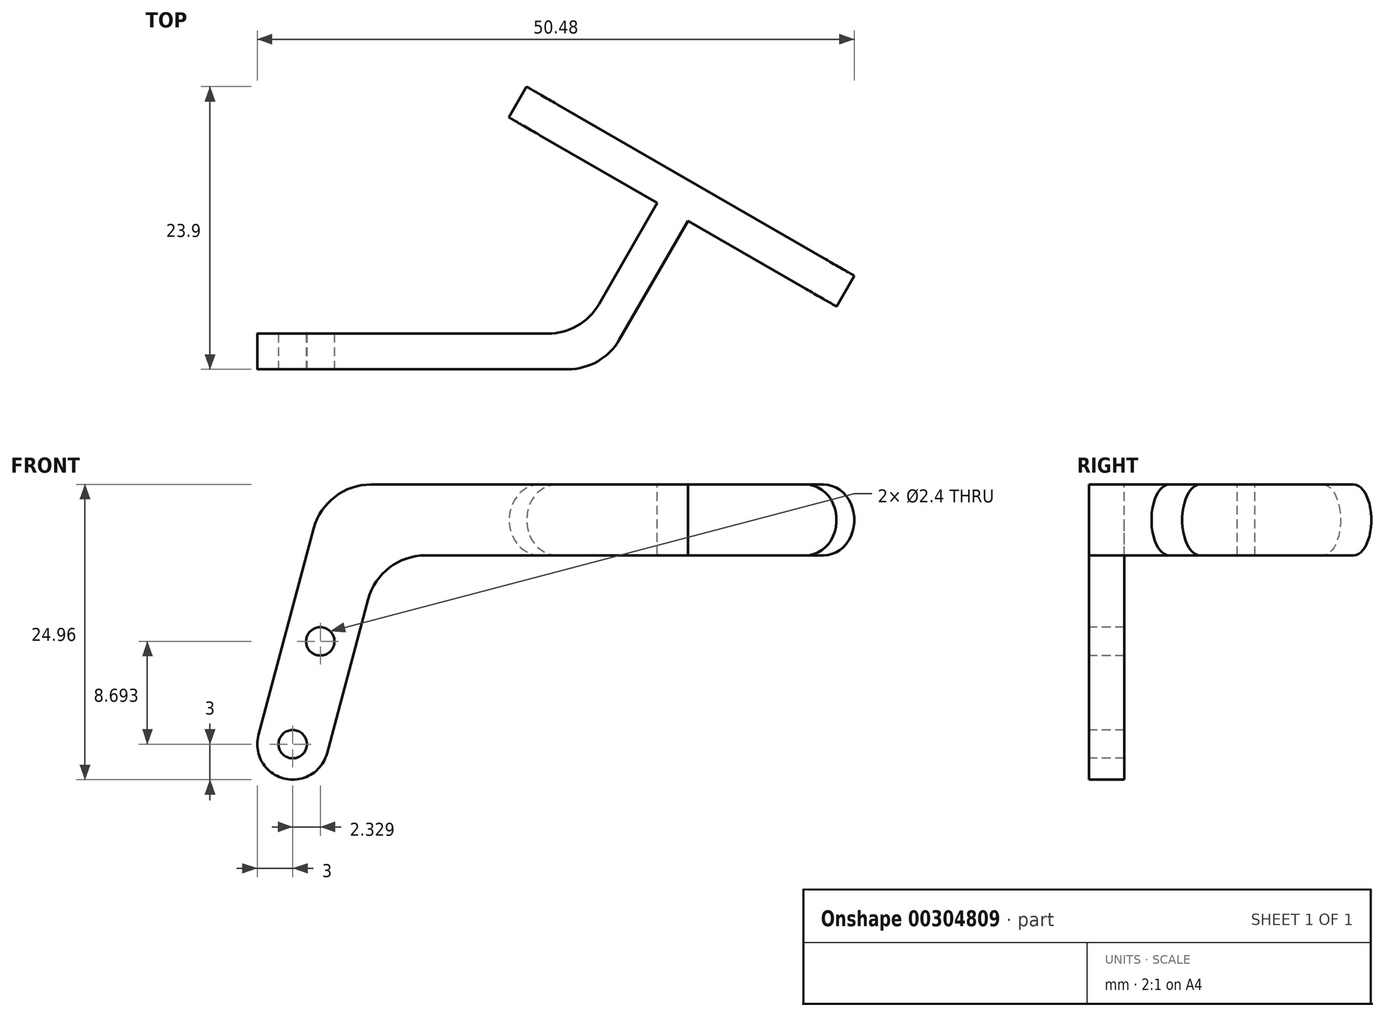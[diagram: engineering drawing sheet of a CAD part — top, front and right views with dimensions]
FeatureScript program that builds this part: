
annotation { "Feature Type Name" : "Feature", "Feature Type Description" : "" }
export const myFeature = defineFeature(function(context is Context, id is Id, definition is map)
    precondition{}
    {
        {
            var Q0;
            Q0=qCreatedBy(makeId("Top.planeOp"),FACE);
            var sketch = newSketch(context, id + "F0", { "sketchPlane" : qUnion([Q0])});
            skLineSegment(sketch, "E0.bottom", {"start": v(-41.87, -28.47) * mm, "end": v(81.94, -28.47) * mm});
            skLineSegment(sketch, "E0.top", {"start": v(-41.87, 130.62) * mm, "end": v(81.94, 130.62) * mm});
            skLineSegment(sketch, "E0.left", {"start": v(-41.87, -28.47) * mm, "end": v(-41.87, 130.62) * mm});
            skLineSegment(sketch, "E0.right", {"start": v(81.94, -28.47) * mm, "end": v(81.94, 130.62) * mm});
            skLineSegment(sketch, "E1", {"start": v(194.3, 41.37) * mm, "end": v(212.32, 28.75) * mm});
            skLineSegment(sketch, "E2", {"start": v(183.43, 8.54) * mm, "end": v(183.43, 37.28) * mm});
            skLineSegment(sketch, "E3", {"start": v(196.02, 43.83) * mm, "end": v(214.04, 31.21) * mm});
            skLineSegment(sketch, "E4", {"start": v(214.04, 31.21) * mm, "end": v(212.32, 28.75) * mm});
            skPoint(sketch, "E5", {"position": v(211.58, 32.93) * mm});
            skPoint(sketch, "E6", {"position": v(199.3, 41.54) * mm});
            skPoint(sketch, "E7.visualSharp", {"position": v(186.43, 46.88) * mm});
            skArc(sketch, "E7.filletArc", {"start": v(194.3, 41.37) * mm, "mid": v(189.12, 41.71) * mm, "end": v(186.43, 37.28) * mm});
            skArc(sketch, "E8", {"start": v(196.02, 43.83) * mm, "mid": v(187.74, 44.37) * mm, "end": v(183.43, 37.28) * mm});
            skLineSegment(sketch, "E9", {"start": v(134.5, 0.54) * mm, "end": v(178.43, 0.54) * mm});
            skLineSegment(sketch, "E10", {"start": v(134.5, 0.54) * mm, "end": v(134.5, 3.54) * mm});
            skLineSegment(sketch, "E11", {"start": v(134.5, 3.54) * mm, "end": v(178.43, 3.54) * mm});
            skPoint(sketch, "E12.visualSharp", {"position": v(183.43, 3.54) * mm});
            skArc(sketch, "E12.filletArc", {"start": v(178.43, 3.54) * mm, "mid": v(181.96, 5) * mm, "end": v(183.43, 8.54) * mm});
            skArc(sketch, "E13", {"start": v(178.43, 0.54) * mm, "mid": v(184.09, 2.88) * mm, "end": v(186.43, 8.54) * mm});
            skLineSegment(sketch, "E14.trimOffspring", {"start": v(186.43, 8.54) * mm, "end": v(186.43, 37.28) * mm});
            skPoint(sketch, "E15.orphan", {"position": v(186.43, 0.54) * mm});
            skLineSegment(sketch, "E16", {"start": v(18.3, 21.29) * mm, "end": v(45.98, 5.3) * mm});
            skLineSegment(sketch, "E17", {"start": v(19.77, 23.9) * mm, "end": v(47.48, 7.9) * mm});
            skLineSegment(sketch, "E18", {"start": v(47.48, 7.9) * mm, "end": v(45.98, 5.3) * mm});
            skPoint(sketch, "E19", {"position": v(44.89, 9.4) * mm});
            skPoint(sketch, "E20", {"position": v(22.37, 22.4) * mm});
            skLineSegment(sketch, "E21.trimOffspring", {"start": v(27.63, 2.5) * mm, "end": v(33.43, 12.55) * mm});
            skLineSegment(sketch, "E22", {"start": v(18.3, 21.29) * mm, "end": v(19.77, 23.9) * mm});
            skPoint(sketch, "E23", {"position": v(33.63, 15.9) * mm});
            skLineSegment(sketch, "E24", {"start": v(0, 0) * mm, "end": v(23.3, 0) * mm});
            skLineSegment(sketch, "E25", {"start": v(0, 0) * mm, "end": v(0, 3) * mm});
            skLineSegment(sketch, "E26", {"start": v(0, 3) * mm, "end": v(21.56, 3) * mm});
            skLineSegment(sketch, "E27.trimOffspring", {"start": v(25.9, 5.5) * mm, "end": v(30.83, 14.05) * mm});
            skPoint(sketch, "E28.visualSharp", {"position": v(24.45, 3) * mm});
            skArc(sketch, "E28.filletArc", {"start": v(21.56, 3) * mm, "mid": v(24.06, 3.67) * mm, "end": v(25.9, 5.5) * mm});
            skPoint(sketch, "E29.visualSharp", {"position": v(26.18, 0) * mm});
            skArc(sketch, "E29.filletArc", {"start": v(23.3, 0) * mm, "mid": v(25.8, 0.67) * mm, "end": v(27.63, 2.5) * mm});
            skLineSegment(sketch, "E30.bottom", {"start": v(0, 0) * mm, "end": v(-9.27, 0) * mm});
            skLineSegment(sketch, "E30.top", {"start": v(0, 3) * mm, "end": v(-9.27, 3) * mm});
            skLineSegment(sketch, "E30.right", {"start": v(-9.27, 0) * mm, "end": v(-9.27, 3) * mm});
            skSolve(sketch);
        }
        {
            var Q0;
            Q0=qCreatedBy(makeId("Front.planeOp"),FACE);
            var sketch = newSketch(context, id + "F1", { "sketchPlane" : qUnion([Q0])});
            skPoint(sketch, "E31", {"position": v(0, -28.2) * mm});
            skLineSegment(sketch, "E32", {"start": v(-2.9, -27.42) * mm, "end": v(1.79, -9.95) * mm});
            skLineSegment(sketch, "E33", {"start": v(2.9, -28.98) * mm, "end": v(6.39, -15.95) * mm});
            skLineSegment(sketch, "E34", {"start": v(11.22, -12.24) * mm, "end": v(56.5, -12.24) * mm});
            skLineSegment(sketch, "E35.trimOffspring", {"start": v(6.61, -6.24) * mm, "end": v(56.5, -6.24) * mm});
            skArc(sketch, "E36", {"start": v(-2.9, -27.42) * mm, "mid": v(-0.78, -31.1) * mm, "end": v(2.9, -28.98) * mm});
            skPoint(sketch, "E37.visualSharp", {"position": v(2.78, -6.24) * mm});
            skArc(sketch, "E37.filletArc", {"start": v(6.61, -6.24) * mm, "mid": v(3.57, -7.27) * mm, "end": v(1.79, -9.95) * mm});
            skPoint(sketch, "E38.visualSharp", {"position": v(7.38, -12.24) * mm});
            skArc(sketch, "E38.filletArc", {"start": v(11.22, -12.24) * mm, "mid": v(8.18, -13.27) * mm, "end": v(6.39, -15.95) * mm});
            skLineSegment(sketch, "E39", {"start": v(56.5, -6.24) * mm, "end": v(56.5, -12.24) * mm});
            skLineSegment(sketch, "E40", {"start": v(0, -28.2) * mm, "end": v(-3.5, -41.24) * mm});
            skLineSegment(sketch, "E41", {"start": v(0, -28.2) * mm, "end": v(2.33, -19.5) * mm});
            skPoint(sketch, "E42", {"position": v(2.33, -19.5) * mm});
            skPoint(sketch, "E43", {"position": v(-3.5, -41.24) * mm});
            skCircle(sketch, "E44", {"center": v(0, -28.2) * mm, "radius": 1.2 * mm});
            skCircle(sketch, "E45", {"center": v(2.33, -19.5) * mm, "radius": 1.2 * mm});
            skSolve(sketch);
        }
        {
            var Q0;
            Q0=qCreatedBy(makeId("Front.planeOp"),FACE);
            cPlane(context, id + "F2", {"entities" : qUnion([Q0]), "cplaneType" : CPlaneType.OFFSET, "offset" : 1 * mm, "width" : 150 * mm, "height" : 150 * mm});
        }
        {
            var Q0;
            Q0=qCreatedBy(id+"F2.planeOp",FACE);
            var sketch = newSketch(context, id + "F3", { "sketchPlane" : qUnion([Q0])});
            skCircle(sketch, "E46", {"center": v(0, -28.2) * mm, "radius": 1.5 * mm});
            skSolve(sketch);
        }
        {
            var Q0;
            Q0 = qSketchRegion(id + "F3", true);
            extrude(context, id + "F4", {"entities" : qUnion([Q0]), "depth" : 5 * mm});
        }
        {
            var Q0;
            Q0 = qSketchRegion(id + "F1", true);
            extrude(context, id + "F5", {"entities" : qUnion([Q0]), "operationType" : NewBodyOperationType.ADD, "oppositeDirection" : true, "depth" : 100 * mm});
        }
        {
            var Q0;
            Q0 = qSketchRegion(id + "F0", true);
            extrude(context, id + "F6", {"entities" : qUnion([Q0]), "operationType" : NewBodyOperationType.REMOVE, "endBound" : BoundingType.THROUGH_ALL, "oppositeDirection" : true, "depth" : 25 * mm});
        }
        {
            var Q0;
            Q0=makeQuery(id+"F6.boolean.opBoolean","INTERSECT",EDGE,{"derivedFrom":[makeQuery(id+"F5.opExtrude","SWEPT_FACE",FACE,{"disambiguationData":[OSD([sQuery(id+"F1.wireOp",EDGE,"E35.trimOffspring")])]}),makeQuery(id+"F6.opExtrude","SWEPT_FACE",FACE,{"disambiguationData":[OSD([sQuery(id+"F0.wireOp",EDGE,"E22")])]})]});
            var Q1;
            Q1=makeQuery(id+"F6.boolean.opBoolean","INTERSECT",EDGE,{"derivedFrom":[makeQuery(id+"F5.opExtrude","SWEPT_FACE",FACE,{"disambiguationData":[OSD([sQuery(id+"F1.wireOp",EDGE,"E35.trimOffspring")])]}),makeQuery(id+"F6.opExtrude","SWEPT_FACE",FACE,{"disambiguationData":[OSD([sQuery(id+"F0.wireOp",EDGE,"E18")])]})]});
            var Q2;
            Q2=makeQuery(id+"F6.boolean.opBoolean","INTERSECT",EDGE,{"derivedFrom":[makeQuery(id+"F5.opExtrude","SWEPT_FACE",FACE,{"disambiguationData":[OSD([sQuery(id+"F1.wireOp",EDGE,"E34")])]}),makeQuery(id+"F6.opExtrude","SWEPT_FACE",FACE,{"disambiguationData":[OSD([sQuery(id+"F0.wireOp",EDGE,"E18")])]})]});
            var Q3;
            Q3=makeQuery(id+"F6.boolean.opBoolean","INTERSECT",EDGE,{"derivedFrom":[makeQuery(id+"F5.opExtrude","SWEPT_FACE",FACE,{"disambiguationData":[OSD([sQuery(id+"F1.wireOp",EDGE,"E34")])]}),makeQuery(id+"F6.opExtrude","SWEPT_FACE",FACE,{"disambiguationData":[OSD([sQuery(id+"F0.wireOp",EDGE,"E22")])]})]});
            fillet(context, id + "F7", {"entities" : qUnion([Q0, Q1, Q2, Q3]), "radius" : 3 * mm, "tangentPropagation" : true, "allowEdgeOverflow" : false});
        }
    });
